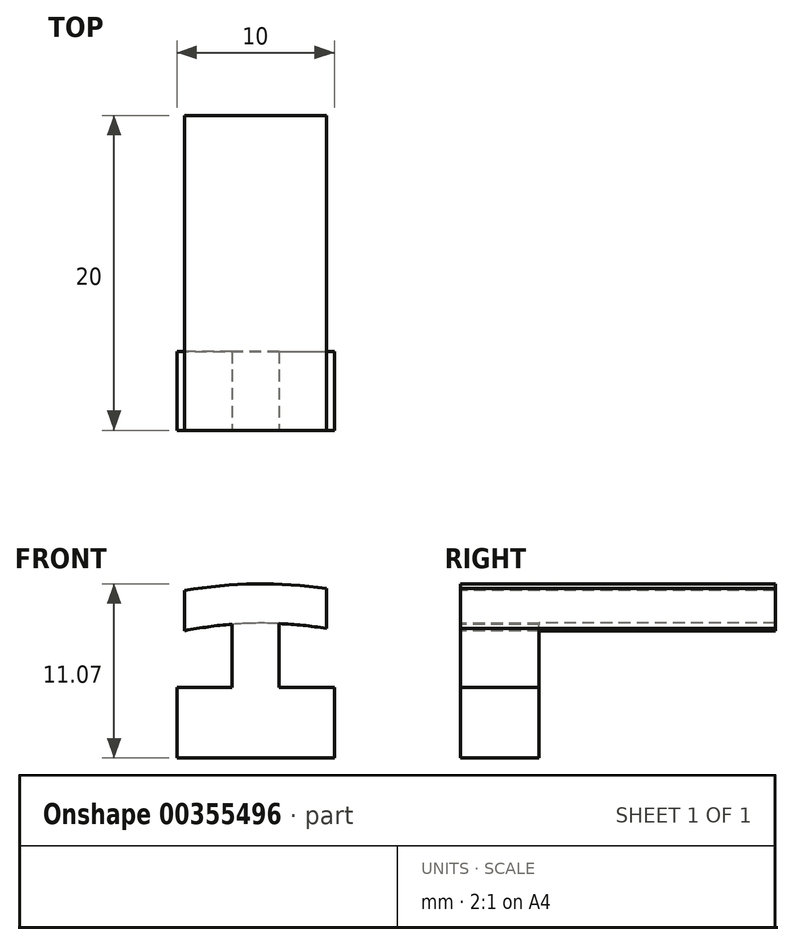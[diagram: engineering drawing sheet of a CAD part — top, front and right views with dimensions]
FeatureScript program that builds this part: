
annotation { "Feature Type Name" : "Feature", "Feature Type Description" : "" }
export const myFeature = defineFeature(function(context is Context, id is Id, definition is map)
    precondition{}
    {
        {
            var Q0;
            Q0=qCreatedBy(makeId("Front.planeOp"),FACE);
            var sketch = newSketch(context, id + "F0", { "sketchPlane" : qUnion([Q0])});
            skLineSegment(sketch, "E0", {"start": v(-30.55, 20.93) * mm, "end": v(-34.05, 20.93) * mm});
            skLineSegment(sketch, "E1", {"start": v(-34.05, 20.93) * mm, "end": v(-34.05, 16.43) * mm});
            skPoint(sketch, "E2.center.orphan", {"position": v(-28.67, 0) * mm});
            skArc(sketch, "E3", {"start": v(-24.55, 24.66) * mm, "mid": v(-29.06, 25) * mm, "end": v(-33.55, 24.52) * mm});
            skLineSegment(sketch, "E4", {"start": v(-30.55, 20.93) * mm, "end": v(-30.55, 24.93) * mm});
            skArc(sketch, "E5.0", {"start": v(-24.55, 27.2) * mm, "mid": v(-29.06, 27.5) * mm, "end": v(-33.55, 27.06) * mm});
            skLineSegment(sketch, "E6.MirrorCS", {"start": v(-27.55, 20.93) * mm, "end": v(-27.55, 24.93) * mm});
            skLineSegment(sketch, "E7.MirrorCS", {"start": v(-27.55, 20.93) * mm, "end": v(-24.05, 20.93) * mm});
            skLineSegment(sketch, "E8", {"start": v(-33.55, 27.06) * mm, "end": v(-33.55, 24.52) * mm});
            skLineSegment(sketch, "E9.MirrorCS", {"start": v(-24.55, 27.2) * mm, "end": v(-24.55, 24.52) * mm});
            skLineSegment(sketch, "E10", {"start": v(-27.55, 24.93) * mm, "end": v(-27.55, 24.98) * mm});
            skLineSegment(sketch, "E11", {"start": v(-34.05, 16.43) * mm, "end": v(-24.05, 16.43) * mm});
            skLineSegment(sketch, "E12", {"start": v(-24.05, 20.93) * mm, "end": v(-24.05, 16.43) * mm});
            skPoint(sketch, "E13.start.orphan", {"position": v(-29.05, 20.93) * mm});
            skSolve(sketch);
        }
        {
            var Q0;
            {var subQ0=sQuery(id+"F0.wireOp",EDGE,"E5.0");Q0=makeQuery(id+"F0.imprint","IMPRINT",FACE,{"disambiguationData":[TD([[makeQuery(id+"F0.imprint","IMPRINT",EDGE,{"derivedFrom":subQ0}),1.0]])]});}
            extrude(context, id + "F1", {"entities" : qUnion([Q0]), "oppositeDirection" : true, "depth" : 20 * mm});
        }
        {
            var Q0;
            Q0=makeQuery(id+"F0.imprint","IMPRINT",FACE,{"disambiguationData":[TD([[makeQuery(id+"F0.imprint","IMPRINT",EDGE,{"derivedFrom":sQuery(id+"F0.wireOp",EDGE,"E0")}),1.0]])]});
            extrude(context, id + "F2", {"entities" : qUnion([Q0]), "operationType" : NewBodyOperationType.ADD, "oppositeDirection" : true, "depth" : 5 * mm});
        }
    });
